FCSTD DOCUMENT  (FreeCAD 0.22R35466 (Git))
Label: mobile_base_assembly
License: All rights reserved
LicenseURL: http://en.wikipedia.org/wiki/All_rights_reserved
objects: App::Link×6, App::DocumentObjectGroup×3, PartDesign::CoordinateSystem×1, App::FeaturePython×1, App::Part×1
note: 1 computed .brp shape members not serialized (recipe doc carries the construction recipe); baked Part::Feature solids carry a one-line shape summary decoded from their .brp
EXTERNAL_REF file=drill_press_mobile_base.FCStd obj=Part002
EXTERNAL_REF file=drill_press_mobile_base.FCStd obj=Part003
EXTERNAL_REF file=drill_press_mobile_base.FCStd obj=Spreadsheet

FEATURE [App::DocumentObjectGroup] Parts
FEATURE [PartDesign::CoordinateSystem] LCS_Origin
  AttacherType = Attacher::AttachEngine3D
  MapMode = 2
  Support = -> [X_Axis]
FEATURE [App::DocumentObjectGroup] Constraints
FEATURE [App::FeaturePython] Variables  # WARN: FeaturePython — macro-defined, semantics opaque (R4)
  Type = App::PropertyContainer
FEATURE [App::DocumentObjectGroup] Configurations
FEATURE [App::Link] storage_cabinet
  LinkedObject = -> <external drill_press_mobile_base.FCStd>#Part002
FEATURE [App::Link] storage_cabinet_drawer
  LinkPlacement = pos=(0,12,18) rot=(0,0,1;0rad)
  LinkedObject = -> <external drill_press_mobile_base.FCStd>#Part003
  Placement = pos=(0,12,18) rot=(0,0,1;0rad)
  expr: .Placement.Base.z = 18 mm
FEATURE [App::Link] storage_cabinet_drawer_2
  LinkPlacement = pos=(0,12,118) rot=(0,0,1;0rad)
  LinkedObject = -> <external drill_press_mobile_base.FCStd>#Part003
  Placement = pos=(0,12,118) rot=(0,0,1;0rad)
  expr: .Placement.Base.z = drill_press_mobile_base#Spreadsheet.ply_18 + 1 * (drill_press_mobile_base#Spreadsheet.ply_6 + drill_press_mobile_base#Spreadsheet.sc_drawer_height + 6 mm)
FEATURE [App::Link] storage_cabinet_drawer001  label="storage_cabinet_drawer_3"
  LinkPlacement = pos=(0,12,218) rot=(0,0,1;0rad)
  LinkedObject = -> <external drill_press_mobile_base.FCStd>#Part003
  Placement = pos=(0,12,218) rot=(0,0,1;0rad)
  expr: .Placement.Base.z = drill_press_mobile_base#Spreadsheet.ply_18 + 2 * (drill_press_mobile_base#Spreadsheet.ply_6 + drill_press_mobile_base#Spreadsheet.sc_drawer_height + 6 mm)
FEATURE [App::Link] storage_cabinet_1  label="storage_cabinet_drawer_4"
  LinkPlacement = pos=(0,12,318) rot=(0,0,1;0rad)
  LinkedObject = -> <external drill_press_mobile_base.FCStd>#Part003
  Placement = pos=(0,12,318) rot=(0,0,1;0rad)
  expr: .Placement.Base.z = drill_press_mobile_base#Spreadsheet.ply_18 + 3 * (drill_press_mobile_base#Spreadsheet.ply_6 + drill_press_mobile_base#Spreadsheet.sc_drawer_height + 6 mm)
FEATURE [App::Link] storage_cabinet_drawer_1
  LinkPlacement = pos=(0,12,418) rot=(0,0,1;0rad)
  LinkedObject = -> <external drill_press_mobile_base.FCStd>#Part003
  Placement = pos=(0,12,418) rot=(0,0,1;0rad)
  expr: .Placement.Base.z = drill_press_mobile_base#Spreadsheet.ply_18 + 4 * (drill_press_mobile_base#Spreadsheet.ply_6 + drill_press_mobile_base#Spreadsheet.sc_drawer_height + 6 mm)
FEATURE [App::Part] Assembly
  AssemblyType = Part::Link
  Group = -> [LCS_Origin,Constraints,Variables,Configurations,storage_cabinet,storage_cabinet_drawer,storage_cabinet_drawer_2,storage_cabinet_drawer001,storage_cabinet_1,storage_cabinet_drawer_1]
  Origin = -> Origin
  Type = Assembly

RESOLVED EXTERNAL PARTS (link-assembly join: the EXTERNAL_REF files above that resolve inside this repo's crawl, each included once):
---- part drill_press_mobile_base.FCStd = doc fcstd_b64e72e19532 (111313 chars; too large to inline — full recipe in that document) ----
